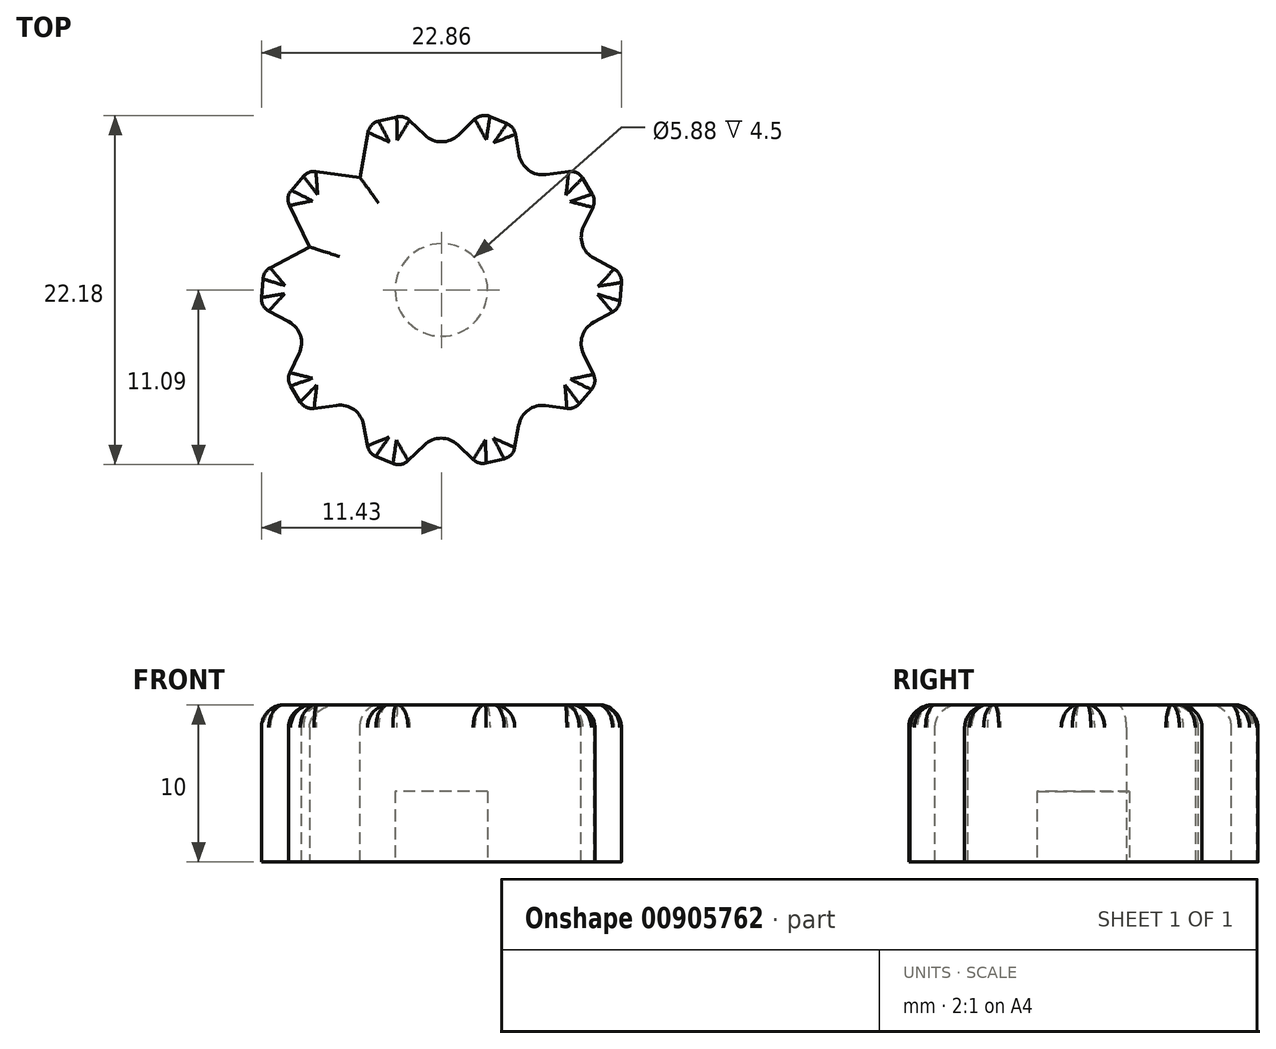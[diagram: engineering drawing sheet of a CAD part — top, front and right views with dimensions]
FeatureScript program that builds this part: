
annotation { "Feature Type Name" : "Feature", "Feature Type Description" : "" }
export const myFeature = defineFeature(function(context is Context, id is Id, definition is map)
    precondition{}
    {
        {
            var Q0;
            Q0=qCreatedBy(makeId("Top.planeOp"),FACE);
            var sketch = newSketch(context, id + "F0", { "sketchPlane" : qUnion([Q0])});
            skCircle(sketch, "E0", {"center": v(0, 0) * mm, "radius": 8.5 * mm});
            skLineSegment(sketch, "E1.right", {"start": v(-11.3, 1.18) * mm, "end": v(-11.48, -1.06) * mm});
            skPoint(sketch, "E1.middle", {"position": v(-8.5, 0) * mm});
            skLineSegment(sketch, "E2", {"start": v(-11.48, -1.06) * mm, "end": v(-7.98, -2.94) * mm});
            skLineSegment(sketch, "E3", {"start": v(-11.3, 1.18) * mm, "end": v(-7.96, 2.97) * mm});
            skPoint(sketch, "E1.left.end.orphan", {"position": v(-5.7, -1.18) * mm});
            skPoint(sketch, "E4.orphan", {"position": v(-5.52, 1.06) * mm});
            skCircle(sketch, "E5", {"center": v(0, 0) * mm, "radius": 2.94 * mm});
            skSolve(sketch);
        }
        {
            var Q0;
            {var subQ0=sQuery(id+"F0.wireOp",EDGE,"E0");var subQ1=makeQuery(id+"F0.imprint","INTERSECT",VERTEX,{"derivedFrom":[subQ0,sQuery(id+"F0.wireOp",EDGE,"E2")]});Q0=makeQuery(id+"F0.imprint","IMPRINT",FACE,{"disambiguationData":[TD([[makeQuery(id+"F0.imprint","IMPRINT",EDGE,{"disambiguationData":[TD([[subQ1,1.0]])],"derivedFrom":subQ0}),1.0]])]});}
            var Q1;
            Q1=makeQuery(id+"F0.imprint","IMPRINT",FACE,{"disambiguationData":[TD([[makeQuery(id+"F0.imprint","IMPRINT",EDGE,{"derivedFrom":sQuery(id+"F0.wireOp",EDGE,"E5")}),1.0]])]});
            extrude(context, id + "F1", {"entities" : qUnion([Q0, Q1]), "depth" : 10 * mm, "offsetDistance" : 25 * mm});
        }
        {
            var Q0;
            Q0=makeQuery(id+"F0.imprint","IMPRINT",FACE,{"disambiguationData":[TD([[makeQuery(id+"F0.imprint","IMPRINT",EDGE,{"derivedFrom":sQuery(id+"F0.wireOp",EDGE,"E1.right")}),1.0]])]});
            extrude(context, id + "F2", {"entities" : qUnion([Q0]), "depth" : 10 * mm, "offsetDistance" : 25 * mm});
        }
        {
            var Q0;
            Q0=qCreatedBy(makeId("Front.planeOp"),FACE);
            var sketch = newSketch(context, id + "F3", { "sketchPlane" : qUnion([Q0])});
            skLineSegment(sketch, "E6", {"start": v(0, 0) * mm, "end": v(0, 10.02) * mm});
            skSolve(sketch);
        }
        {
            var Q0;
            Q0=makeQuery(id+"F2.opExtrude","SWEPT_EDGE",EDGE,{"disambiguationData":[OSD([sQuery(id+"F0.wireOp",EDGE,"E1.right"),sQuery(id+"F0.wireOp",EDGE,"E3")])]});
            var Q1;
            Q1=makeQuery(id+"F2.opExtrude","SWEPT_EDGE",EDGE,{"disambiguationData":[OSD([sQuery(id+"F0.wireOp",EDGE,"E1.right"),sQuery(id+"F0.wireOp",EDGE,"E2")])]});
            fillet(context, id + "F4", {"entities" : qUnion([Q0, Q1]), "radius" : 0.89 * mm, "tangentPropagation" : true, "allowEdgeOverflow" : false});
        }
        {
            var Q0;
            Q0=makeQuery(id+"F2.opExtrude","SWEPT_BODY",BODY,{"disambiguationData":[OSD([sQuery(id+"F0.wireOp",EDGE,"E0"),sQuery(id+"F0.wireOp",EDGE,"E1.right"),sQuery(id+"F0.wireOp",EDGE,"E2"),sQuery(id+"F0.wireOp",EDGE,"E3")])]});
            var Q1;
            Q1=sQuery(id+"F3.wireOp",EDGE,"E6");
            circularPattern(context, id + "F5", {"entities" : qUnion([Q0]), "axis" : qUnion([Q1]), "angle" : 360 * degree, "instanceCount" : 10, "equalSpace" : true});
        }
        {
            var Q0;
            Q0=makeQuery(id+"F2.opExtrude","SWEPT_BODY",BODY,{"disambiguationData":[OSD([sQuery(id+"F0.wireOp",EDGE,"E0"),sQuery(id+"F0.wireOp",EDGE,"E1.right"),sQuery(id+"F0.wireOp",EDGE,"E2"),sQuery(id+"F0.wireOp",EDGE,"E3")])]});
            var Q1;
            Q1=makeQuery(id+"F5.opPattern","COPY",BODY,{"derivedFrom":makeQuery(id+"F2.opExtrude","SWEPT_BODY",BODY,{"disambiguationData":[OSD([sQuery(id+"F0.wireOp",EDGE,"E0"),sQuery(id+"F0.wireOp",EDGE,"E1.right"),sQuery(id+"F0.wireOp",EDGE,"E2"),sQuery(id+"F0.wireOp",EDGE,"E3")])]}),"instanceName":"1"});
            var Q2;
            Q2=makeQuery(id+"F5.opPattern","COPY",BODY,{"derivedFrom":makeQuery(id+"F2.opExtrude","SWEPT_BODY",BODY,{"disambiguationData":[OSD([sQuery(id+"F0.wireOp",EDGE,"E0"),sQuery(id+"F0.wireOp",EDGE,"E1.right"),sQuery(id+"F0.wireOp",EDGE,"E2"),sQuery(id+"F0.wireOp",EDGE,"E3")])]}),"instanceName":"2"});
            var Q3;
            Q3=makeQuery(id+"F5.opPattern","COPY",BODY,{"derivedFrom":makeQuery(id+"F2.opExtrude","SWEPT_BODY",BODY,{"disambiguationData":[OSD([sQuery(id+"F0.wireOp",EDGE,"E0"),sQuery(id+"F0.wireOp",EDGE,"E1.right"),sQuery(id+"F0.wireOp",EDGE,"E2"),sQuery(id+"F0.wireOp",EDGE,"E3")])]}),"instanceName":"3"});
            var Q4;
            Q4=makeQuery(id+"F5.opPattern","COPY",BODY,{"derivedFrom":makeQuery(id+"F2.opExtrude","SWEPT_BODY",BODY,{"disambiguationData":[OSD([sQuery(id+"F0.wireOp",EDGE,"E0"),sQuery(id+"F0.wireOp",EDGE,"E1.right"),sQuery(id+"F0.wireOp",EDGE,"E2"),sQuery(id+"F0.wireOp",EDGE,"E3")])]}),"instanceName":"4"});
            var Q5;
            Q5=makeQuery(id+"F5.opPattern","COPY",BODY,{"derivedFrom":makeQuery(id+"F2.opExtrude","SWEPT_BODY",BODY,{"disambiguationData":[OSD([sQuery(id+"F0.wireOp",EDGE,"E0"),sQuery(id+"F0.wireOp",EDGE,"E1.right"),sQuery(id+"F0.wireOp",EDGE,"E2"),sQuery(id+"F0.wireOp",EDGE,"E3")])]}),"instanceName":"5"});
            var Q6;
            Q6=makeQuery(id+"F5.opPattern","COPY",BODY,{"derivedFrom":makeQuery(id+"F2.opExtrude","SWEPT_BODY",BODY,{"disambiguationData":[OSD([sQuery(id+"F0.wireOp",EDGE,"E0"),sQuery(id+"F0.wireOp",EDGE,"E1.right"),sQuery(id+"F0.wireOp",EDGE,"E2"),sQuery(id+"F0.wireOp",EDGE,"E3")])]}),"instanceName":"6"});
            var Q7;
            Q7=makeQuery(id+"F5.opPattern","COPY",BODY,{"derivedFrom":makeQuery(id+"F2.opExtrude","SWEPT_BODY",BODY,{"disambiguationData":[OSD([sQuery(id+"F0.wireOp",EDGE,"E0"),sQuery(id+"F0.wireOp",EDGE,"E1.right"),sQuery(id+"F0.wireOp",EDGE,"E2"),sQuery(id+"F0.wireOp",EDGE,"E3")])]}),"instanceName":"7"});
            var Q8;
            Q8=makeQuery(id+"F1.opExtrude","SWEPT_BODY",BODY,{"disambiguationData":[OSD([sQuery(id+"F0.wireOp",EDGE,"E0")])]});
            var Q9;
            Q9=makeQuery(id+"F5.opPattern","COPY",BODY,{"derivedFrom":makeQuery(id+"F2.opExtrude","SWEPT_BODY",BODY,{"disambiguationData":[OSD([sQuery(id+"F0.wireOp",EDGE,"E0"),sQuery(id+"F0.wireOp",EDGE,"E1.right"),sQuery(id+"F0.wireOp",EDGE,"E2"),sQuery(id+"F0.wireOp",EDGE,"E3")])]}),"instanceName":"8"});
            var Q10;
            Q10=makeQuery(id+"F5.opPattern","COPY",BODY,{"derivedFrom":makeQuery(id+"F2.opExtrude","SWEPT_BODY",BODY,{"disambiguationData":[OSD([sQuery(id+"F0.wireOp",EDGE,"E0"),sQuery(id+"F0.wireOp",EDGE,"E1.right"),sQuery(id+"F0.wireOp",EDGE,"E2"),sQuery(id+"F0.wireOp",EDGE,"E3")])]}),"instanceName":"9"});
            booleanBodies(context, id + "F6", {"operationType" : BooleanOperationType.UNION, "tools" : qUnion([Q0, Q1, Q2, Q3, Q4, Q5, Q6, Q7, Q8, Q9, Q10])});
        }
        {
            var Q0;
            Q0=makeQuery(id+"F6.opBoolean","INTERSECT",EDGE,{"derivedFrom":[makeQuery(id+"F2.opExtrude","SWEPT_FACE",FACE,{"disambiguationData":[OSD([sQuery(id+"F0.wireOp",EDGE,"E2")])]}),makeQuery(id+"F5.opPattern","COPY",FACE,{"derivedFrom":makeQuery(id+"F2.opExtrude","SWEPT_FACE",FACE,{"disambiguationData":[OSD([sQuery(id+"F0.wireOp",EDGE,"E3")])]}),"instanceName":"1"})]});
            var Q1;
            Q1=makeQuery(id+"F6.opBoolean","INTERSECT",EDGE,{"derivedFrom":[makeQuery(id+"F5.opPattern","COPY",FACE,{"derivedFrom":makeQuery(id+"F2.opExtrude","SWEPT_FACE",FACE,{"disambiguationData":[OSD([sQuery(id+"F0.wireOp",EDGE,"E2")])]}),"instanceName":"1"}),makeQuery(id+"F5.opPattern","COPY",FACE,{"derivedFrom":makeQuery(id+"F2.opExtrude","SWEPT_FACE",FACE,{"disambiguationData":[OSD([sQuery(id+"F0.wireOp",EDGE,"E3")])]}),"instanceName":"2"})]});
            var Q2;
            Q2=makeQuery(id+"F6.opBoolean","INTERSECT",EDGE,{"derivedFrom":[makeQuery(id+"F5.opPattern","COPY",FACE,{"derivedFrom":makeQuery(id+"F2.opExtrude","SWEPT_FACE",FACE,{"disambiguationData":[OSD([sQuery(id+"F0.wireOp",EDGE,"E2")])]}),"instanceName":"2"}),makeQuery(id+"F5.opPattern","COPY",FACE,{"derivedFrom":makeQuery(id+"F2.opExtrude","SWEPT_FACE",FACE,{"disambiguationData":[OSD([sQuery(id+"F0.wireOp",EDGE,"E3")])]}),"instanceName":"3"})]});
            var Q3;
            Q3=makeQuery(id+"F6.opBoolean","INTERSECT",EDGE,{"derivedFrom":[makeQuery(id+"F5.opPattern","COPY",FACE,{"derivedFrom":makeQuery(id+"F2.opExtrude","SWEPT_FACE",FACE,{"disambiguationData":[OSD([sQuery(id+"F0.wireOp",EDGE,"E2")])]}),"instanceName":"3"}),makeQuery(id+"F5.opPattern","COPY",FACE,{"derivedFrom":makeQuery(id+"F2.opExtrude","SWEPT_FACE",FACE,{"disambiguationData":[OSD([sQuery(id+"F0.wireOp",EDGE,"E3")])]}),"instanceName":"4"})]});
            var Q4;
            Q4=makeQuery(id+"F6.opBoolean","INTERSECT",EDGE,{"derivedFrom":[makeQuery(id+"F5.opPattern","COPY",FACE,{"derivedFrom":makeQuery(id+"F2.opExtrude","SWEPT_FACE",FACE,{"disambiguationData":[OSD([sQuery(id+"F0.wireOp",EDGE,"E2")])]}),"instanceName":"4"}),makeQuery(id+"F5.opPattern","COPY",FACE,{"derivedFrom":makeQuery(id+"F2.opExtrude","SWEPT_FACE",FACE,{"disambiguationData":[OSD([sQuery(id+"F0.wireOp",EDGE,"E3")])]}),"instanceName":"5"})]});
            var Q5;
            Q5=makeQuery(id+"F6.opBoolean","INTERSECT",EDGE,{"derivedFrom":[makeQuery(id+"F5.opPattern","COPY",FACE,{"derivedFrom":makeQuery(id+"F2.opExtrude","SWEPT_FACE",FACE,{"disambiguationData":[OSD([sQuery(id+"F0.wireOp",EDGE,"E2")])]}),"instanceName":"5"}),makeQuery(id+"F5.opPattern","COPY",FACE,{"derivedFrom":makeQuery(id+"F2.opExtrude","SWEPT_FACE",FACE,{"disambiguationData":[OSD([sQuery(id+"F0.wireOp",EDGE,"E3")])]}),"instanceName":"6"})]});
            var Q6;
            Q6=makeQuery(id+"F6.opBoolean","INTERSECT",EDGE,{"derivedFrom":[makeQuery(id+"F5.opPattern","COPY",FACE,{"derivedFrom":makeQuery(id+"F2.opExtrude","SWEPT_FACE",FACE,{"disambiguationData":[OSD([sQuery(id+"F0.wireOp",EDGE,"E2")])]}),"instanceName":"6"}),makeQuery(id+"F5.opPattern","COPY",FACE,{"derivedFrom":makeQuery(id+"F2.opExtrude","SWEPT_FACE",FACE,{"disambiguationData":[OSD([sQuery(id+"F0.wireOp",EDGE,"E3")])]}),"instanceName":"7"})]});
            var Q7;
            Q7=makeQuery(id+"F6.opBoolean","INTERSECT",EDGE,{"derivedFrom":[makeQuery(id+"F5.opPattern","COPY",FACE,{"derivedFrom":makeQuery(id+"F2.opExtrude","SWEPT_FACE",FACE,{"disambiguationData":[OSD([sQuery(id+"F0.wireOp",EDGE,"E2")])]}),"instanceName":"7"}),makeQuery(id+"F5.opPattern","COPY",FACE,{"derivedFrom":makeQuery(id+"F2.opExtrude","SWEPT_FACE",FACE,{"disambiguationData":[OSD([sQuery(id+"F0.wireOp",EDGE,"E3")])]}),"instanceName":"8"})]});
            var Q8;
            Q8=makeQuery(id+"F6.opBoolean","INTERSECT",EDGE,{"derivedFrom":[makeQuery(id+"F2.opExtrude","SWEPT_FACE",FACE,{"disambiguationData":[OSD([sQuery(id+"F0.wireOp",EDGE,"E3")])]}),makeQuery(id+"F5.opPattern","COPY",FACE,{"derivedFrom":makeQuery(id+"F2.opExtrude","SWEPT_FACE",FACE,{"disambiguationData":[OSD([sQuery(id+"F0.wireOp",EDGE,"E2")])]}),"instanceName":"8"})]});
            fillet(context, id + "F7", {"entities" : qUnion([Q0, Q1, Q2, Q3, Q4, Q5, Q6, Q7, Q8]), "radius" : 1.53 * mm, "tangentPropagation" : true, "allowEdgeOverflow" : false});
        }
        {
            var Q0;
            Q0=makeQuery(id+"F0.imprint","IMPRINT",FACE,{"disambiguationData":[TD([[makeQuery(id+"F0.imprint","IMPRINT",EDGE,{"derivedFrom":sQuery(id+"F0.wireOp",EDGE,"E5")}),1.0]])]});
            extrude(context, id + "F8", {"entities" : qUnion([Q0]), "operationType" : NewBodyOperationType.REMOVE, "depth" : 4.5 * mm, "offsetDistance" : 25 * mm});
        }
        {
            var Q0;
            {var subQ0=sQuery(id+"F0.wireOp",EDGE,"E0");var subQ1=makeQuery(id+"F2.opExtrude","CAP_FACE",FACE,{"disambiguationData":[OSD([subQ0,sQuery(id+"F0.wireOp",EDGE,"E1.right"),sQuery(id+"F0.wireOp",EDGE,"E2"),sQuery(id+"F0.wireOp",EDGE,"E3")])],"isStart":false});Q0=makeQuery(id+"F6.opBoolean","MERGE",FACE,{"derivedFrom":[makeQuery(id+"F1.opExtrude","CAP_FACE",FACE,{"disambiguationData":[OSD([subQ0])],"isStart":false}),subQ1,makeQuery(id+"F5.opPattern","COPY",FACE,{"derivedFrom":subQ1,"instanceName":"1"}),makeQuery(id+"F5.opPattern","COPY",FACE,{"derivedFrom":subQ1,"instanceName":"2"}),makeQuery(id+"F5.opPattern","COPY",FACE,{"derivedFrom":subQ1,"instanceName":"3"}),makeQuery(id+"F5.opPattern","COPY",FACE,{"derivedFrom":subQ1,"instanceName":"4"}),makeQuery(id+"F5.opPattern","COPY",FACE,{"derivedFrom":subQ1,"instanceName":"5"}),makeQuery(id+"F5.opPattern","COPY",FACE,{"derivedFrom":subQ1,"instanceName":"6"}),makeQuery(id+"F5.opPattern","COPY",FACE,{"derivedFrom":subQ1,"instanceName":"7"}),makeQuery(id+"F5.opPattern","COPY",FACE,{"derivedFrom":subQ1,"instanceName":"8"}),makeQuery(id+"F5.opPattern","COPY",FACE,{"derivedFrom":subQ1,"instanceName":"9"})]});}
            fillet(context, id + "F9", {"entities" : qUnion([Q0]), "radius" : 1.45 * mm, "tangentPropagation" : true, "allowEdgeOverflow" : false});
        }
    });
